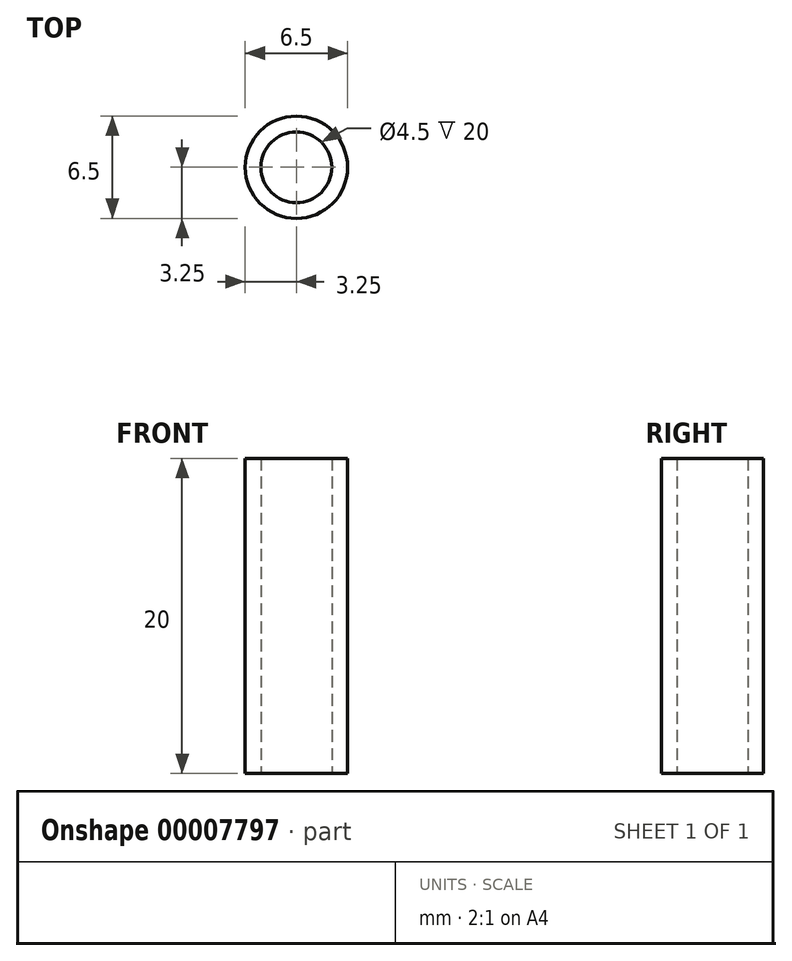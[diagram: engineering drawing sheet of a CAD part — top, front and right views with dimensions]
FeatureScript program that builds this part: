
annotation { "Feature Type Name" : "Feature", "Feature Type Description" : "" }
export const myFeature = defineFeature(function(context is Context, id is Id, definition is map)
    precondition{}
    {
        {
            var Q0;
            Q0=qCreatedBy(makeId("Top.planeOp"),FACE);
            var sketch = newSketch(context, id + "F0", { "sketchPlane" : qUnion([Q0])});
            skCircle(sketch, "E0", {"center": v(0, 0) * mm, "radius": 2.25 * mm});
            skCircle(sketch, "E1", {"center": v(0, 0) * mm, "radius": 3.25 * mm});
            skSolve(sketch);
        }
        {
            var Q0;
            Q0=makeQuery(id+"F0.imprint","IMPRINT",FACE,{"disambiguationData":[TD([[makeQuery(id+"F0.imprint","IMPRINT",EDGE,{"derivedFrom":sQuery(id+"F0.wireOp",EDGE,"E0")}),-1.0]])]});
            extrude(context, id + "F1", {"entities" : qUnion([Q0]), "depth" : 20 * mm});
        }
    });
